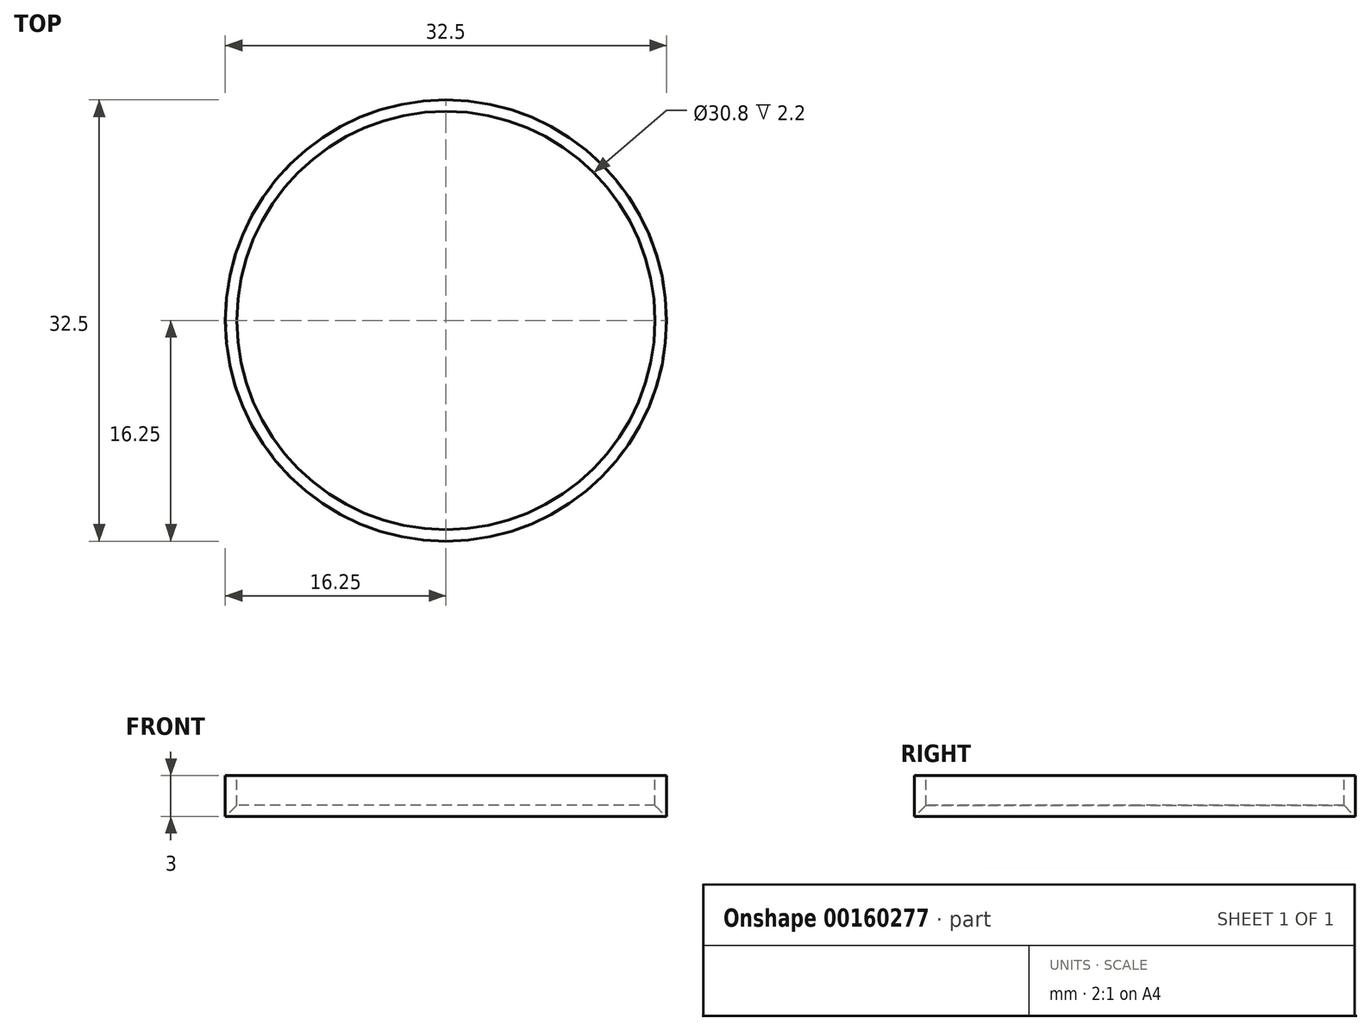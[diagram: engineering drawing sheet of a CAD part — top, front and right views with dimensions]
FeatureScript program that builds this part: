
annotation { "Feature Type Name" : "Feature", "Feature Type Description" : "" }
export const myFeature = defineFeature(function(context is Context, id is Id, definition is map)
    precondition{}
    {
        {
            var Q0;
            Q0=qCreatedBy(makeId("Top.planeOp"),FACE);
            var sketch = newSketch(context, id + "F0", { "sketchPlane" : qUnion([Q0])});
            skCircle(sketch, "E0", {"center": v(0, 0) * mm, "radius": 16.25 * mm});
            skSolve(sketch);
        }
        {
            var Q0;
            Q0=qSketchRegion(id+"F0",true);
            extrude(context, id + "F1", {"entities" : qUnion([Q0]), "depth" : 3 * mm});
        }
        {
            var Q0;
            Q0=makeQuery(id+"F1.opExtrude","CAP_FACE",FACE,{"disambiguationData":[OSD([sQuery(id+"F0.wireOp",EDGE,"E0")])],"isStart":false});
            var sketch = newSketch(context, id + "F2", { "sketchPlane" : qUnion([Q0])});
            skCircle(sketch, "E1", {"center": v(0, 0) * mm, "radius": 15.4 * mm});
            skSolve(sketch);
        }
        {
            var Q0;
            Q0=qSketchRegion(id+"F2",true);
            extrude(context, id + "F3", {"entities" : qUnion([Q0]), "operationType" : NewBodyOperationType.REMOVE, "endBound" : BoundingType.THROUGH_ALL, "oppositeDirection" : true, "depth" : 25 * mm});
        }
        {
            var Q0;
            Q0=makeQuery(id+"F3.boolean.opBoolean","COPY",EDGE,{"derivedFrom":makeQuery(id+"F3.opExtrude","CAP_EDGE",EDGE,{"disambiguationData":[OSD([sQuery(id+"F2.wireOp",EDGE,"E1")])],"isStart":true})});
            var Q1;
            Q1=makeQuery(id+"F3.boolean.opBoolean","INTERSECT",EDGE,{"derivedFrom":[makeQuery(id+"F1.opExtrude","CAP_FACE",FACE,{"disambiguationData":[OSD([sQuery(id+"F0.wireOp",EDGE,"E0")])],"isStart":true}),makeQuery(id+"F3.opExtrude","SWEPT_FACE",FACE,{"disambiguationData":[OSD([sQuery(id+"F2.wireOp",EDGE,"E1")])]})]});
            chamfer(context, id + "F4", {"entities" : qUnion([Q0, Q1]), "width" : 0.8 * mm, "tangentPropagation" : true});
        }
    });
